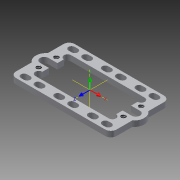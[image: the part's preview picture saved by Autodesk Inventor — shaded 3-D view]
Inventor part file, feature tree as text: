
AUTODESK INVENTOR PART (.ipt)
format: ipt  version: 2015 (Build 190159000, 159)  size: 328,192 bytes
history: native  units: in
note: dims shown in document units (in); Inventor stores cm internally (conversion verified against a paired STEP export)
features: hole x19, sketch x11, other x9, extrude x1, imported_body x1, projected_geometry x1
ambient origin geometry x8: Origin, YZ Plane, XZ Plane, XY Plane, X Axis, Y Axis, Z Axis, Center Point
bodies: Solid1 (feature_tree)
feature tree (42):
  other  "User Library-575112.sat1"
  other  "UCS1"
  sketch  "Sketch2"  dims[d0=0.0in d1=0.063in d2=0.0in d3=0.0in d4=0.0in d5=0.0in d6=1.0in d7=0.0in]
  sketch  "Sketch3"  dims[d8=0.104in d9=0.276in d10=0.375in d11=0.25in d12=0.5635in d13=0.432in d14=0.8108in]
  extrude  "Extrusion1"  Depth=1.0in TaperAngle=0.0deg
  hole  "Hole1"  [1 undecoded]
  hole  "Hole3"  [1 undecoded]
  hole  "Hole5"  [1 undecoded]
  hole  "Hole7"  [1 undecoded]
  hole  "Hole9"  [1 undecoded]
  hole  "Hole11"  [1 undecoded]
  hole  "Hole13"  [1 undecoded]
  hole  "Hole15"  [1 undecoded]
  hole  "Hole17"  [1 undecoded]
  hole  "Hole19"  [1 undecoded]
  imported_body  "Base1"
  projected_geometry  "Projected Loop2"
  sketch  "Sketch4"  dims[d15=0.104in d16=0.2831in d17=0.375in d18=0.25in d19=0.5635in d20=0.3521in d21=120.0deg]
  hole  "Hole2"  [1 undecoded]
  sketch  "Sketch5"  dims[d22=0.104in d23=0.2831in d24=0.375in d25=0.25in d26=0.5635in d27=0.3521in d28=120.0deg]
  hole  "Hole4"  [1 undecoded]
  sketch  "Sketch6"  dims[d29=0.104in d30=0.2831in d31=0.375in d32=0.25in d33=0.5635in d34=0.3521in d35=120.0deg]
  hole  "Hole6"  [1 undecoded]
  sketch  "Sketch7"  dims[d36=0.104in d37=0.2831in d38=0.375in d39=0.25in d40=0.5635in d41=0.3521in d42=120.0deg]
  hole  "Hole8"  [1 undecoded]
  sketch  "Sketch8"  dims[d43=0.104in d44=0.2831in d45=0.375in d46=0.25in d47=0.5635in d48=0.3521in d49=120.0deg]
  hole  "Hole10"  [1 undecoded]
  sketch  "Sketch9"  dims[d50=0.104in d51=0.138in d52=0.375in d53=0.25in d54=0.5635in d55=0.207in d56=120.0deg]
  hole  "Hole12"  [1 undecoded]
  sketch  "Sketch10"  dims[d57=0.104in d58=0.2831in d59=0.375in d60=0.25in d61=0.5635in d62=0.3521in d63=120.0deg]
  hole  "Hole14"  [1 undecoded]
  sketch  "Sketch11"  dims[d64=0.104in d65=0.2831in d66=0.375in d67=0.25in d68=0.5635in d69=0.3521in d70=120.0deg]
  hole  "Hole16"  [1 undecoded]
  sketch  "Sketch12"  dims[d71=0.104in d72=0.2831in d73=0.375in d74=0.25in d75=0.5635in d76=0.3521in d77=120.0deg]
  hole  "Hole18"  [1 undecoded]
  other  "UCS1: YZ Plane"
  other  "UCS1: XZ Plane"
  other  "UCS1: XY Plane"
  other  "UCS1: X Axis"
  other  "UCS1: Y Axis"
  other  "UCS1: Z Axis"
  other  "UCS1: Center Point"
note: 19 required parameter values undecoded (feature->parameter linkage not recoverable at this tier; creation-order binding heuristic only, values carry confidence <= 0.55)
